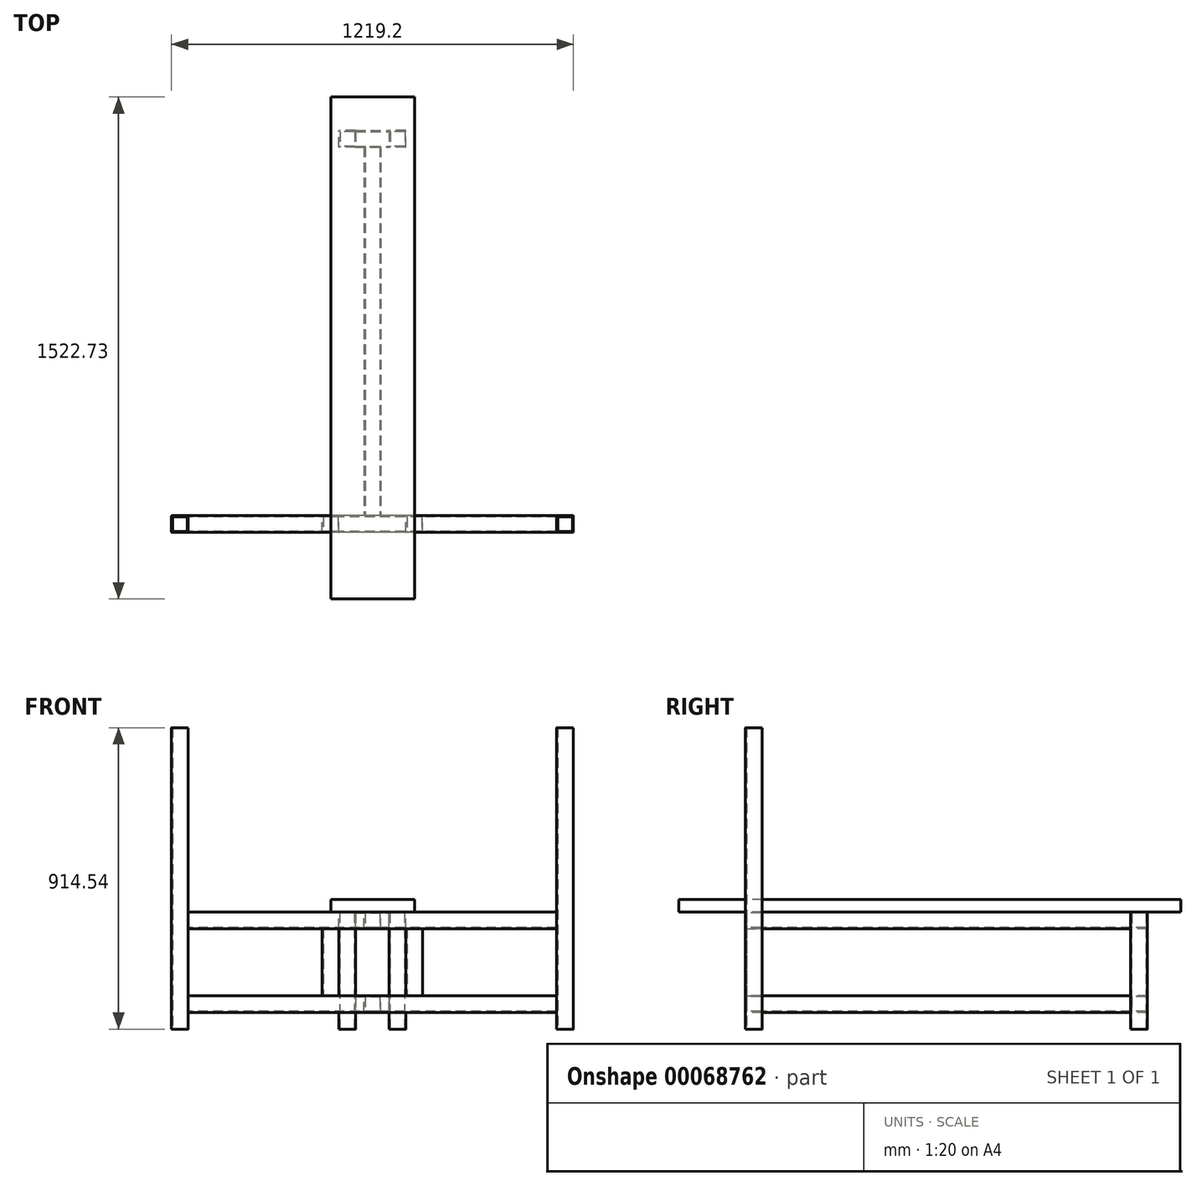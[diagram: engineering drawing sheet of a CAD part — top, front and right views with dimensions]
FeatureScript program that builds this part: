
annotation { "Feature Type Name" : "Feature", "Feature Type Description" : "" }
export const myFeature = defineFeature(function(context is Context, id is Id, definition is map)
    precondition{}
    {
        {
            var Q0;
            Q0=qCreatedBy(makeId("Front.planeOp"),FACE);
            var sketch = newSketch(context, id + "F0", { "sketchPlane" : qUnion([Q0])});
            skLineSegment(sketch, "E0.rect.bottom", {"start": v(24.13, -25.4) * mm, "end": v(-24.13, -25.4) * mm});
            skLineSegment(sketch, "E0.rect.top", {"start": v(24.13, 25.4) * mm, "end": v(-24.13, 25.4) * mm});
            skLineSegment(sketch, "E0.rect.left", {"start": v(25.4, -24.13) * mm, "end": v(25.4, 24.13) * mm});
            skLineSegment(sketch, "E0.rect.right", {"start": v(-25.4, -24.13) * mm, "end": v(-25.4, 24.13) * mm});
            skPoint(sketch, "E0.rect.middle", {"position": v(0, 0) * mm});
            skPoint(sketch, "E1.visualSharp", {"position": v(-25.4, 25.4) * mm});
            skArc(sketch, "E1.filletArc", {"start": v(-24.13, 25.4) * mm, "mid": v(-25.03, 25.03) * mm, "end": v(-25.4, 24.13) * mm});
            skPoint(sketch, "E2.visualSharp", {"position": v(25.4, 25.4) * mm});
            skArc(sketch, "E2.filletArc", {"start": v(25.4, 24.13) * mm, "mid": v(25.03, 25.03) * mm, "end": v(24.13, 25.4) * mm});
            skPoint(sketch, "E3.visualSharp", {"position": v(25.4, -25.4) * mm});
            skArc(sketch, "E3.filletArc", {"start": v(24.13, -25.4) * mm, "mid": v(25.03, -25.03) * mm, "end": v(25.4, -24.13) * mm});
            skPoint(sketch, "E4.visualSharp", {"position": v(-25.4, -25.4) * mm});
            skArc(sketch, "E4.filletArc", {"start": v(-25.4, -24.13) * mm, "mid": v(-25.03, -25.03) * mm, "end": v(-24.13, -25.4) * mm});
            skLineSegment(sketch, "E5.bottom", {"start": v(21.08, 22.35) * mm, "end": v(-21.08, 22.35) * mm});
            skLineSegment(sketch, "E5.top", {"start": v(21.08, -22.35) * mm, "end": v(-21.08, -22.35) * mm});
            skLineSegment(sketch, "E5.left", {"start": v(22.35, 21.08) * mm, "end": v(22.35, -21.08) * mm});
            skLineSegment(sketch, "E5.right", {"start": v(-22.35, 21.08) * mm, "end": v(-22.35, -21.08) * mm});
            skPoint(sketch, "E6.visualSharp", {"position": v(-22.35, 22.35) * mm});
            skArc(sketch, "E6.filletArc", {"start": v(-21.08, 22.35) * mm, "mid": v(-21.98, 21.98) * mm, "end": v(-22.35, 21.08) * mm});
            skPoint(sketch, "E7.visualSharp", {"position": v(22.35, 22.35) * mm});
            skArc(sketch, "E7.filletArc", {"start": v(22.35, 21.08) * mm, "mid": v(21.98, 21.98) * mm, "end": v(21.08, 22.35) * mm});
            skPoint(sketch, "E8.visualSharp", {"position": v(22.35, -22.35) * mm});
            skArc(sketch, "E8.filletArc", {"start": v(21.08, -22.35) * mm, "mid": v(21.98, -21.98) * mm, "end": v(22.35, -21.08) * mm});
            skPoint(sketch, "E9.visualSharp", {"position": v(-22.35, -22.35) * mm});
            skArc(sketch, "E9.filletArc", {"start": v(-22.35, -21.08) * mm, "mid": v(-21.98, -21.98) * mm, "end": v(-21.08, -22.35) * mm});
            skSolve(sketch);
        }
        {
            var Q0;
            Q0=makeQuery(id+"F0.imprint","IMPRINT",FACE,{"disambiguationData":[TD([[makeQuery(id+"F0.imprint","IMPRINT",EDGE,{"derivedFrom":sQuery(id+"F0.wireOp",EDGE,"E0.rect.bottom")}),-1.0]])]});
            extrude(context, id + "F1", {"entities" : qUnion([Q0]), "oppositeDirection" : true, "depth" : 1117.6 * mm});
        }
        {
            var Q0;
            Q0=makeQuery(id+"F1.opExtrude","SWEPT_FACE",FACE,{"disambiguationData":[OSD([sQuery(id+"F0.wireOp",EDGE,"E0.rect.left")])]});
            var sketch = newSketch(context, id + "F2", { "sketchPlane" : qUnion([Q0])});
            skLineSegment(sketch, "E10", {"start": v(1116.6, 0) * mm, "end": v(1169.4, 0) * mm, "construction": true});
            skPoint(sketch, "E10.startSnap0", {"position": v(1117.6, 0) * mm});
            skLineSegment(sketch, "E11", {"start": v(1143, 0) * mm, "end": v(1143, 22.98) * mm, "construction": true});
            skLineSegment(sketch, "E12.rect.bottom", {"start": v(1167.13, -25.4) * mm, "end": v(1118.87, -25.4) * mm});
            skLineSegment(sketch, "E12.rect.top", {"start": v(1167.13, 25.4) * mm, "end": v(1118.87, 25.4) * mm});
            skLineSegment(sketch, "E12.rect.left", {"start": v(1168.4, -24.13) * mm, "end": v(1168.4, 24.13) * mm});
            skLineSegment(sketch, "E12.rect.right", {"start": v(1117.6, -24.13) * mm, "end": v(1117.6, 24.13) * mm});
            skPoint(sketch, "E12.rect.middle", {"position": v(1143, 0) * mm});
            skPoint(sketch, "E13.visualSharp", {"position": v(1117.6, 25.4) * mm});
            skArc(sketch, "E13.filletArc", {"start": v(1118.87, 25.4) * mm, "mid": v(1117.97, 25.03) * mm, "end": v(1117.6, 24.13) * mm});
            skPoint(sketch, "E14.visualSharp", {"position": v(1168.4, 25.4) * mm});
            skArc(sketch, "E14.filletArc", {"start": v(1168.4, 24.13) * mm, "mid": v(1168.03, 25.03) * mm, "end": v(1167.13, 25.4) * mm});
            skPoint(sketch, "E15.visualSharp", {"position": v(1168.4, -25.4) * mm});
            skArc(sketch, "E15.filletArc", {"start": v(1167.13, -25.4) * mm, "mid": v(1168.03, -25.03) * mm, "end": v(1168.4, -24.13) * mm});
            skPoint(sketch, "E16.visualSharp", {"position": v(1117.6, -25.4) * mm});
            skArc(sketch, "E16.filletArc", {"start": v(1117.6, -24.13) * mm, "mid": v(1117.97, -25.03) * mm, "end": v(1118.87, -25.4) * mm});
            skLineSegment(sketch, "E17.bottom", {"start": v(1164.08, 22.35) * mm, "end": v(1121.92, 22.35) * mm});
            skLineSegment(sketch, "E17.top", {"start": v(1164.08, -22.35) * mm, "end": v(1121.92, -22.35) * mm});
            skLineSegment(sketch, "E17.left", {"start": v(1165.35, 21.08) * mm, "end": v(1165.35, -21.08) * mm});
            skLineSegment(sketch, "E17.right", {"start": v(1120.65, 21.08) * mm, "end": v(1120.65, -21.08) * mm});
            skPoint(sketch, "E18.visualSharp", {"position": v(1120.65, 22.35) * mm});
            skArc(sketch, "E18.filletArc", {"start": v(1121.92, 22.35) * mm, "mid": v(1121.02, 21.98) * mm, "end": v(1120.65, 21.08) * mm});
            skPoint(sketch, "E19.visualSharp", {"position": v(1165.35, 22.35) * mm});
            skArc(sketch, "E19.filletArc", {"start": v(1165.35, 21.08) * mm, "mid": v(1164.98, 21.98) * mm, "end": v(1164.08, 22.35) * mm});
            skPoint(sketch, "E20.visualSharp", {"position": v(1165.35, -22.35) * mm});
            skArc(sketch, "E20.filletArc", {"start": v(1164.08, -22.35) * mm, "mid": v(1164.98, -21.98) * mm, "end": v(1165.35, -21.08) * mm});
            skPoint(sketch, "E21.visualSharp", {"position": v(1120.65, -22.35) * mm});
            skArc(sketch, "E21.filletArc", {"start": v(1120.65, -21.08) * mm, "mid": v(1121.02, -21.98) * mm, "end": v(1121.92, -22.35) * mm});
            skSolve(sketch);
        }
        {
            var Q0;
            Q0=makeQuery(id+"F2.imprint","IMPRINT",FACE,{"disambiguationData":[TD([[makeQuery(id+"F2.imprint","IMPRINT",EDGE,{"derivedFrom":sQuery(id+"F2.wireOp",EDGE,"E12.rect.bottom")}),-1.0]])]});
            extrude(context, id + "F3", {"entities" : qUnion([Q0]), "oppositeDirection" : true, "depth" : 76.2 * mm});
        }
        {
            var Q0;
            Q0=makeQuery(id+"F3.opExtrude","CAP_FACE",FACE,{"disambiguationData":[OSD([sQuery(id+"F2.wireOp",EDGE,"E12.rect.bottom"),sQuery(id+"F2.wireOp",EDGE,"E12.rect.top"),sQuery(id+"F2.wireOp",EDGE,"E12.rect.left"),sQuery(id+"F2.wireOp",EDGE,"E12.rect.right"),sQuery(id+"F2.wireOp",EDGE,"E13.filletArc"),sQuery(id+"F2.wireOp",EDGE,"E14.filletArc"),sQuery(id+"F2.wireOp",EDGE,"E15.filletArc"),sQuery(id+"F2.wireOp",EDGE,"E16.filletArc"),sQuery(id+"F2.wireOp",EDGE,"E17.bottom"),sQuery(id+"F2.wireOp",EDGE,"E17.top"),sQuery(id+"F2.wireOp",EDGE,"E17.left"),sQuery(id+"F2.wireOp",EDGE,"E17.right"),sQuery(id+"F2.wireOp",EDGE,"E18.filletArc"),sQuery(id+"F2.wireOp",EDGE,"E19.filletArc"),sQuery(id+"F2.wireOp",EDGE,"E20.filletArc"),sQuery(id+"F2.wireOp",EDGE,"E21.filletArc")])],"isStart":true});
            extrude(context, id + "F4", {"entities" : qUnion([Q0]), "operationType" : NewBodyOperationType.ADD, "depth" : 25.4 * mm});
        }
        {
            var Q0;
            Q0=qCreatedBy(makeId("Front.planeOp"),FACE);
            var sketch = newSketch(context, id + "F5", { "sketchPlane" : qUnion([Q0])});
            skLineSegment(sketch, "E22.rect.bottom", {"start": v(24.13, 228.6) * mm, "end": v(-24.13, 228.6) * mm});
            skLineSegment(sketch, "E22.rect.top", {"start": v(24.13, 279.4) * mm, "end": v(-24.13, 279.4) * mm});
            skLineSegment(sketch, "E22.rect.left", {"start": v(25.4, 229.87) * mm, "end": v(25.4, 278.13) * mm});
            skLineSegment(sketch, "E22.rect.right", {"start": v(-25.4, 229.87) * mm, "end": v(-25.4, 278.13) * mm});
            skPoint(sketch, "E22.rect.middle", {"position": v(0, 254) * mm});
            skPoint(sketch, "E23.visualSharp", {"position": v(-25.4, 279.4) * mm});
            skArc(sketch, "E23.filletArc", {"start": v(-24.13, 279.4) * mm, "mid": v(-25.03, 279.03) * mm, "end": v(-25.4, 278.13) * mm});
            skPoint(sketch, "E24.visualSharp", {"position": v(25.4, 279.4) * mm});
            skArc(sketch, "E24.filletArc", {"start": v(25.4, 278.13) * mm, "mid": v(25.03, 279.03) * mm, "end": v(24.13, 279.4) * mm});
            skPoint(sketch, "E25.visualSharp", {"position": v(25.4, 228.6) * mm});
            skArc(sketch, "E25.filletArc", {"start": v(24.13, 228.6) * mm, "mid": v(25.03, 228.97) * mm, "end": v(25.4, 229.87) * mm});
            skPoint(sketch, "E26.visualSharp", {"position": v(-25.4, 228.6) * mm});
            skArc(sketch, "E26.filletArc", {"start": v(-25.4, 229.87) * mm, "mid": v(-25.03, 228.97) * mm, "end": v(-24.13, 228.6) * mm});
            skLineSegment(sketch, "E27.bottom", {"start": v(21.08, 276.35) * mm, "end": v(-21.08, 276.35) * mm});
            skLineSegment(sketch, "E27.top", {"start": v(21.08, 231.65) * mm, "end": v(-21.08, 231.65) * mm});
            skLineSegment(sketch, "E27.left", {"start": v(22.35, 275.08) * mm, "end": v(22.35, 232.92) * mm});
            skLineSegment(sketch, "E27.right", {"start": v(-22.35, 275.08) * mm, "end": v(-22.35, 232.92) * mm});
            skPoint(sketch, "E28.visualSharp", {"position": v(-22.35, 276.35) * mm});
            skArc(sketch, "E28.filletArc", {"start": v(-21.08, 276.35) * mm, "mid": v(-21.98, 275.98) * mm, "end": v(-22.35, 275.08) * mm});
            skPoint(sketch, "E29.visualSharp", {"position": v(22.35, 276.35) * mm});
            skArc(sketch, "E29.filletArc", {"start": v(22.35, 275.08) * mm, "mid": v(21.98, 275.98) * mm, "end": v(21.08, 276.35) * mm});
            skPoint(sketch, "E30.visualSharp", {"position": v(22.35, 231.65) * mm});
            skArc(sketch, "E30.filletArc", {"start": v(21.08, 231.65) * mm, "mid": v(21.98, 232.02) * mm, "end": v(22.35, 232.92) * mm});
            skPoint(sketch, "E31.visualSharp", {"position": v(-22.35, 231.65) * mm});
            skArc(sketch, "E31.filletArc", {"start": v(-22.35, 232.92) * mm, "mid": v(-21.98, 232.02) * mm, "end": v(-21.08, 231.65) * mm});
            skLineSegment(sketch, "E32", {"start": v(0, 254) * mm, "end": v(-44.9, 254) * mm});
            skSolve(sketch);
        }
        {
            var Q0;
            Q0=makeQuery(id+"F5.imprint","IMPRINT",FACE,{"disambiguationData":[TD([[makeQuery(id+"F5.imprint","IMPRINT",EDGE,{"derivedFrom":sQuery(id+"F5.wireOp",EDGE,"E22.rect.bottom")}),-1.0]])]});
            extrude(context, id + "F6", {"entities" : qUnion([Q0]), "oppositeDirection" : true, "depth" : 1117.6 * mm});
        }
        {
            var Q0;
            Q0=makeQuery(id+"F4.opExtrude","CAP_FACE",FACE,{"disambiguationData":[OSD([sQuery(id+"F2.wireOp",EDGE,"E12.rect.bottom"),sQuery(id+"F2.wireOp",EDGE,"E12.rect.top"),sQuery(id+"F2.wireOp",EDGE,"E12.rect.left"),sQuery(id+"F2.wireOp",EDGE,"E12.rect.right"),sQuery(id+"F2.wireOp",EDGE,"E13.filletArc"),sQuery(id+"F2.wireOp",EDGE,"E14.filletArc"),sQuery(id+"F2.wireOp",EDGE,"E15.filletArc"),sQuery(id+"F2.wireOp",EDGE,"E16.filletArc"),sQuery(id+"F2.wireOp",EDGE,"E17.bottom"),sQuery(id+"F2.wireOp",EDGE,"E17.top"),sQuery(id+"F2.wireOp",EDGE,"E17.left"),sQuery(id+"F2.wireOp",EDGE,"E17.right"),sQuery(id+"F2.wireOp",EDGE,"E18.filletArc"),sQuery(id+"F2.wireOp",EDGE,"E19.filletArc"),sQuery(id+"F2.wireOp",EDGE,"E20.filletArc"),sQuery(id+"F2.wireOp",EDGE,"E21.filletArc")])],"isStart":false});
            var sketch = newSketch(context, id + "F7", { "sketchPlane" : qUnion([Q0])});
            skLineSegment(sketch, "E33.rect.bottom", {"start": v(1167.13, 228.6) * mm, "end": v(1118.87, 228.6) * mm});
            skLineSegment(sketch, "E33.rect.top", {"start": v(1167.13, 279.4) * mm, "end": v(1118.87, 279.4) * mm});
            skLineSegment(sketch, "E33.rect.left", {"start": v(1168.4, 229.87) * mm, "end": v(1168.4, 278.13) * mm});
            skLineSegment(sketch, "E33.rect.right", {"start": v(1117.6, 229.87) * mm, "end": v(1117.6, 278.13) * mm});
            skPoint(sketch, "E33.rect.middle", {"position": v(1143, 254) * mm});
            skPoint(sketch, "E34.visualSharp", {"position": v(1117.6, 279.4) * mm});
            skArc(sketch, "E34.filletArc", {"start": v(1118.87, 279.4) * mm, "mid": v(1117.97, 279.03) * mm, "end": v(1117.6, 278.13) * mm});
            skPoint(sketch, "E35.visualSharp", {"position": v(1168.4, 279.4) * mm});
            skArc(sketch, "E35.filletArc", {"start": v(1168.4, 278.13) * mm, "mid": v(1168.03, 279.03) * mm, "end": v(1167.13, 279.4) * mm});
            skPoint(sketch, "E36.visualSharp", {"position": v(1168.4, 228.6) * mm});
            skArc(sketch, "E36.filletArc", {"start": v(1167.13, 228.6) * mm, "mid": v(1168.03, 228.97) * mm, "end": v(1168.4, 229.87) * mm});
            skPoint(sketch, "E37.visualSharp", {"position": v(1117.6, 228.6) * mm});
            skArc(sketch, "E37.filletArc", {"start": v(1117.6, 229.87) * mm, "mid": v(1117.97, 228.97) * mm, "end": v(1118.87, 228.6) * mm});
            skLineSegment(sketch, "E38.bottom", {"start": v(1164.08, 276.35) * mm, "end": v(1121.92, 276.35) * mm});
            skLineSegment(sketch, "E38.top", {"start": v(1164.08, 231.65) * mm, "end": v(1121.92, 231.65) * mm});
            skLineSegment(sketch, "E38.left", {"start": v(1165.35, 275.08) * mm, "end": v(1165.35, 232.92) * mm});
            skLineSegment(sketch, "E38.right", {"start": v(1120.65, 275.08) * mm, "end": v(1120.65, 232.92) * mm});
            skPoint(sketch, "E39.visualSharp", {"position": v(1120.65, 276.35) * mm});
            skArc(sketch, "E39.filletArc", {"start": v(1121.92, 276.35) * mm, "mid": v(1121.02, 275.98) * mm, "end": v(1120.65, 275.08) * mm});
            skPoint(sketch, "E40.visualSharp", {"position": v(1165.35, 276.35) * mm});
            skArc(sketch, "E40.filletArc", {"start": v(1165.35, 275.08) * mm, "mid": v(1164.98, 275.98) * mm, "end": v(1164.08, 276.35) * mm});
            skPoint(sketch, "E41.visualSharp", {"position": v(1165.35, 231.65) * mm});
            skArc(sketch, "E41.filletArc", {"start": v(1164.08, 231.65) * mm, "mid": v(1164.98, 232.02) * mm, "end": v(1165.35, 232.92) * mm});
            skPoint(sketch, "E42.visualSharp", {"position": v(1120.65, 231.65) * mm});
            skArc(sketch, "E42.filletArc", {"start": v(1120.65, 232.92) * mm, "mid": v(1121.02, 232.02) * mm, "end": v(1121.92, 231.65) * mm});
            skSolve(sketch);
        }
        {
            var Q0;
            Q0=makeQuery(id+"F7.imprint","IMPRINT",FACE,{"disambiguationData":[TD([[makeQuery(id+"F7.imprint","IMPRINT",EDGE,{"derivedFrom":sQuery(id+"F7.wireOp",EDGE,"E33.rect.top")}),1.0]])]});
            extrude(context, id + "F8", {"entities" : qUnion([Q0]), "oppositeDirection" : true, "depth" : 101.6 * mm});
        }
        {
            var Q0;
            Q0=makeQuery(id+"F8.opExtrude","SWEPT_FACE",FACE,{"disambiguationData":[OSD([sQuery(id+"F7.wireOp",EDGE,"E33.rect.top")])]});
            var sketch = newSketch(context, id + "F9", { "sketchPlane" : qUnion([Q0])});
            skPoint(sketch, "E43.endSnap0", {"position": v(50.8, 1143) * mm});
            skPoint(sketch, "E44", {"position": v(-76.2, 1143) * mm});
            skPoint(sketch, "E45", {"position": v(76.2, 1143) * mm});
            skLineSegment(sketch, "E46.rect.bottom", {"start": v(-52.07, 1117.6) * mm, "end": v(-100.33, 1117.6) * mm});
            skLineSegment(sketch, "E46.rect.top", {"start": v(-52.07, 1168.4) * mm, "end": v(-100.33, 1168.4) * mm});
            skLineSegment(sketch, "E46.rect.left", {"start": v(-50.8, 1118.87) * mm, "end": v(-50.8, 1167.13) * mm});
            skLineSegment(sketch, "E46.rect.right", {"start": v(-101.6, 1118.87) * mm, "end": v(-101.6, 1167.13) * mm});
            skPoint(sketch, "E47.visualSharp", {"position": v(-101.6, 1168.4) * mm});
            skArc(sketch, "E47.filletArc", {"start": v(-100.33, 1168.4) * mm, "mid": v(-101.23, 1168.03) * mm, "end": v(-101.6, 1167.13) * mm});
            skPoint(sketch, "E48.visualSharp", {"position": v(-50.8, 1168.4) * mm});
            skArc(sketch, "E48.filletArc", {"start": v(-50.8, 1167.13) * mm, "mid": v(-51.17, 1168.03) * mm, "end": v(-52.07, 1168.4) * mm});
            skPoint(sketch, "E49.visualSharp", {"position": v(-50.8, 1117.6) * mm});
            skArc(sketch, "E49.filletArc", {"start": v(-52.07, 1117.6) * mm, "mid": v(-51.17, 1117.97) * mm, "end": v(-50.8, 1118.87) * mm});
            skPoint(sketch, "E50.visualSharp", {"position": v(-101.6, 1117.6) * mm});
            skArc(sketch, "E50.filletArc", {"start": v(-101.6, 1118.87) * mm, "mid": v(-101.23, 1117.97) * mm, "end": v(-100.33, 1117.6) * mm});
            skLineSegment(sketch, "E51.bottom", {"start": v(-55.12, 1165.35) * mm, "end": v(-97.28, 1165.35) * mm});
            skLineSegment(sketch, "E51.top", {"start": v(-55.12, 1120.65) * mm, "end": v(-97.28, 1120.65) * mm});
            skLineSegment(sketch, "E51.left", {"start": v(-53.85, 1164.08) * mm, "end": v(-53.85, 1121.92) * mm});
            skLineSegment(sketch, "E51.right", {"start": v(-98.55, 1164.08) * mm, "end": v(-98.55, 1121.92) * mm});
            skPoint(sketch, "E52.visualSharp", {"position": v(-98.55, 1165.35) * mm});
            skArc(sketch, "E52.filletArc", {"start": v(-97.28, 1165.35) * mm, "mid": v(-98.18, 1164.98) * mm, "end": v(-98.55, 1164.08) * mm});
            skPoint(sketch, "E53.visualSharp", {"position": v(-53.85, 1165.35) * mm});
            skArc(sketch, "E53.filletArc", {"start": v(-53.85, 1164.08) * mm, "mid": v(-54.22, 1164.98) * mm, "end": v(-55.12, 1165.35) * mm});
            skPoint(sketch, "E54.visualSharp", {"position": v(-53.85, 1120.65) * mm});
            skArc(sketch, "E54.filletArc", {"start": v(-55.12, 1120.65) * mm, "mid": v(-54.22, 1121.02) * mm, "end": v(-53.85, 1121.92) * mm});
            skPoint(sketch, "E55.visualSharp", {"position": v(-98.55, 1120.65) * mm});
            skArc(sketch, "E55.filletArc", {"start": v(-98.55, 1121.92) * mm, "mid": v(-98.18, 1121.02) * mm, "end": v(-97.28, 1120.65) * mm});
            skLineSegment(sketch, "E56.rect.bottom", {"start": v(100.33, 1117.6) * mm, "end": v(52.04, 1117.6) * mm});
            skLineSegment(sketch, "E56.rect.top", {"start": v(100.33, 1168.4) * mm, "end": v(52.04, 1168.4) * mm});
            skLineSegment(sketch, "E56.rect.left", {"start": v(101.6, 1118.87) * mm, "end": v(101.6, 1167.13) * mm});
            skLineSegment(sketch, "E56.rect.right", {"start": v(50.77, 1118.87) * mm, "end": v(50.77, 1167.13) * mm});
            skPoint(sketch, "E56.rect.middle", {"position": v(76.18, 1143) * mm});
            skPoint(sketch, "E57.visualSharp", {"position": v(50.77, 1168.4) * mm});
            skArc(sketch, "E57.filletArc", {"start": v(52.04, 1168.4) * mm, "mid": v(51.14, 1168.03) * mm, "end": v(50.77, 1167.13) * mm});
            skPoint(sketch, "E58.visualSharp", {"position": v(101.6, 1168.4) * mm});
            skArc(sketch, "E58.filletArc", {"start": v(101.6, 1167.13) * mm, "mid": v(101.23, 1168.03) * mm, "end": v(100.33, 1168.4) * mm});
            skPoint(sketch, "E59.visualSharp", {"position": v(101.6, 1117.6) * mm});
            skArc(sketch, "E59.filletArc", {"start": v(100.33, 1117.6) * mm, "mid": v(101.23, 1117.97) * mm, "end": v(101.6, 1118.87) * mm});
            skPoint(sketch, "E60.visualSharp", {"position": v(50.77, 1117.6) * mm});
            skArc(sketch, "E60.filletArc", {"start": v(50.77, 1118.87) * mm, "mid": v(51.14, 1117.97) * mm, "end": v(52.04, 1117.6) * mm});
            skLineSegment(sketch, "E61.bottom", {"start": v(97.25, 1165.35) * mm, "end": v(55.09, 1165.35) * mm});
            skLineSegment(sketch, "E61.top", {"start": v(97.25, 1120.65) * mm, "end": v(55.09, 1120.65) * mm});
            skLineSegment(sketch, "E61.left", {"start": v(98.52, 1164.08) * mm, "end": v(98.52, 1121.92) * mm});
            skLineSegment(sketch, "E61.right", {"start": v(53.82, 1164.08) * mm, "end": v(53.82, 1121.92) * mm});
            skPoint(sketch, "E62.visualSharp", {"position": v(53.82, 1165.35) * mm});
            skArc(sketch, "E62.filletArc", {"start": v(55.09, 1165.35) * mm, "mid": v(54.19, 1164.98) * mm, "end": v(53.82, 1164.08) * mm});
            skPoint(sketch, "E63.visualSharp", {"position": v(98.52, 1165.35) * mm});
            skArc(sketch, "E63.filletArc", {"start": v(98.52, 1164.08) * mm, "mid": v(98.15, 1164.98) * mm, "end": v(97.25, 1165.35) * mm});
            skPoint(sketch, "E64.visualSharp", {"position": v(98.52, 1120.65) * mm});
            skArc(sketch, "E64.filletArc", {"start": v(97.25, 1120.65) * mm, "mid": v(98.15, 1121.02) * mm, "end": v(98.52, 1121.92) * mm});
            skPoint(sketch, "E65.visualSharp", {"position": v(53.82, 1120.65) * mm});
            skArc(sketch, "E65.filletArc", {"start": v(53.82, 1121.92) * mm, "mid": v(54.19, 1121.02) * mm, "end": v(55.09, 1120.65) * mm});
            skSolve(sketch);
        }
        {
            var Q0;
            Q0=makeQuery(id+"F9.imprint","IMPRINT",FACE,{"disambiguationData":[TD([[makeQuery(id+"F9.imprint","IMPRINT",EDGE,{"derivedFrom":sQuery(id+"F9.wireOp",EDGE,"E46.rect.bottom")}),-1.0]])]});
            var Q1;
            Q1=makeQuery(id+"F9.imprint","IMPRINT",FACE,{"disambiguationData":[TD([[makeQuery(id+"F9.imprint","IMPRINT",EDGE,{"derivedFrom":sQuery(id+"F9.wireOp",EDGE,"E56.rect.bottom")}),-1.0]])]});
            extrude(context, id + "F10", {"entities" : qUnion([Q0, Q1]), "oppositeDirection" : true, "depth" : 355.6 * mm});
        }
        {
            var Q0;
            Q0=qCreatedBy(makeId("Right.planeOp"),FACE);
            var sketch = newSketch(context, id + "F11", { "sketchPlane" : qUnion([Q0])});
            skLineSegment(sketch, "E66", {"start": v(0, 0) * mm, "end": v(-225.93, 0) * mm});
            skLineSegment(sketch, "E67", {"start": v(0, 0) * mm, "end": v(0, 287.4) * mm});
            skLineSegment(sketch, "E68", {"start": v(0, 254) * mm, "end": v(-244.97, 254) * mm});
            skLineSegment(sketch, "E69.rect.bottom", {"start": v(-1.27, -25.4) * mm, "end": v(-49.53, -25.4) * mm});
            skLineSegment(sketch, "E69.rect.top", {"start": v(-1.27, 25.4) * mm, "end": v(-49.53, 25.4) * mm});
            skLineSegment(sketch, "E69.rect.left", {"start": v(0, -24.13) * mm, "end": v(0, 24.13) * mm});
            skLineSegment(sketch, "E69.rect.right", {"start": v(-50.8, -24.13) * mm, "end": v(-50.8, 24.13) * mm});
            skPoint(sketch, "E69.rect.middle", {"position": v(-25.4, 0) * mm});
            skPoint(sketch, "E70.visualSharp", {"position": v(-50.8, 25.4) * mm});
            skArc(sketch, "E70.filletArc", {"start": v(-49.53, 25.4) * mm, "mid": v(-50.43, 25.03) * mm, "end": v(-50.8, 24.13) * mm});
            skPoint(sketch, "E71.visualSharp", {"position": v(0, 25.4) * mm});
            skArc(sketch, "E71.filletArc", {"start": v(0, 24.13) * mm, "mid": v(-0.37, 25.03) * mm, "end": v(-1.27, 25.4) * mm});
            skPoint(sketch, "E72.visualSharp", {"position": v(0, -25.4) * mm});
            skArc(sketch, "E72.filletArc", {"start": v(-1.27, -25.4) * mm, "mid": v(-0.37, -25.03) * mm, "end": v(0, -24.13) * mm});
            skPoint(sketch, "E73.visualSharp", {"position": v(-50.8, -25.4) * mm});
            skArc(sketch, "E73.filletArc", {"start": v(-50.8, -24.13) * mm, "mid": v(-50.43, -25.03) * mm, "end": v(-49.53, -25.4) * mm});
            skLineSegment(sketch, "E74.bottom", {"start": v(-4.32, 22.35) * mm, "end": v(-46.48, 22.35) * mm});
            skLineSegment(sketch, "E74.top", {"start": v(-4.32, -22.35) * mm, "end": v(-46.48, -22.35) * mm});
            skLineSegment(sketch, "E74.left", {"start": v(-3.05, 21.08) * mm, "end": v(-3.05, -21.08) * mm});
            skLineSegment(sketch, "E74.right", {"start": v(-47.75, 21.08) * mm, "end": v(-47.75, -21.08) * mm});
            skPoint(sketch, "E75.visualSharp", {"position": v(-47.75, 22.35) * mm});
            skArc(sketch, "E75.filletArc", {"start": v(-46.48, 22.35) * mm, "mid": v(-47.38, 21.98) * mm, "end": v(-47.75, 21.08) * mm});
            skPoint(sketch, "E76.visualSharp", {"position": v(-3.05, 22.35) * mm});
            skArc(sketch, "E76.filletArc", {"start": v(-3.05, 21.08) * mm, "mid": v(-3.42, 21.98) * mm, "end": v(-4.32, 22.35) * mm});
            skPoint(sketch, "E77.visualSharp", {"position": v(-3.05, -22.35) * mm});
            skArc(sketch, "E77.filletArc", {"start": v(-4.32, -22.35) * mm, "mid": v(-3.42, -21.98) * mm, "end": v(-3.05, -21.08) * mm});
            skPoint(sketch, "E78.visualSharp", {"position": v(-47.75, -22.35) * mm});
            skArc(sketch, "E78.filletArc", {"start": v(-47.75, -21.08) * mm, "mid": v(-47.38, -21.98) * mm, "end": v(-46.48, -22.35) * mm});
            skLineSegment(sketch, "E79.rect.bottom", {"start": v(-1.27, 228.74) * mm, "end": v(-49.53, 228.74) * mm});
            skLineSegment(sketch, "E79.rect.top", {"start": v(-1.27, 279.54) * mm, "end": v(-49.53, 279.54) * mm});
            skLineSegment(sketch, "E79.rect.left", {"start": v(0, 230.01) * mm, "end": v(0, 278.27) * mm});
            skLineSegment(sketch, "E79.rect.right", {"start": v(-50.8, 230.01) * mm, "end": v(-50.8, 278.27) * mm});
            skPoint(sketch, "E79.rect.middle", {"position": v(-25.4, 254.14) * mm});
            skPoint(sketch, "E80.visualSharp", {"position": v(-50.8, 279.54) * mm});
            skArc(sketch, "E80.filletArc", {"start": v(-49.53, 279.54) * mm, "mid": v(-50.43, 279.17) * mm, "end": v(-50.8, 278.27) * mm});
            skPoint(sketch, "E81.visualSharp", {"position": v(0, 279.54) * mm});
            skArc(sketch, "E81.filletArc", {"start": v(0, 278.27) * mm, "mid": v(-0.37, 279.17) * mm, "end": v(-1.27, 279.54) * mm});
            skPoint(sketch, "E82.visualSharp", {"position": v(0, 228.74) * mm});
            skArc(sketch, "E82.filletArc", {"start": v(-1.27, 228.74) * mm, "mid": v(-0.37, 229.11) * mm, "end": v(0, 230.01) * mm});
            skPoint(sketch, "E83.visualSharp", {"position": v(-50.8, 228.74) * mm});
            skArc(sketch, "E83.filletArc", {"start": v(-50.8, 230.01) * mm, "mid": v(-50.43, 229.11) * mm, "end": v(-49.53, 228.74) * mm});
            skLineSegment(sketch, "E84.bottom", {"start": v(-4.32, 276.5) * mm, "end": v(-46.48, 276.5) * mm});
            skLineSegment(sketch, "E84.top", {"start": v(-4.32, 231.79) * mm, "end": v(-46.48, 231.79) * mm});
            skLineSegment(sketch, "E84.left", {"start": v(-3.05, 275.22) * mm, "end": v(-3.05, 233.06) * mm});
            skLineSegment(sketch, "E84.right", {"start": v(-47.75, 275.22) * mm, "end": v(-47.75, 233.06) * mm});
            skPoint(sketch, "E85.visualSharp", {"position": v(-47.75, 276.5) * mm});
            skArc(sketch, "E85.filletArc", {"start": v(-46.48, 276.5) * mm, "mid": v(-47.38, 276.12) * mm, "end": v(-47.75, 275.22) * mm});
            skPoint(sketch, "E86.visualSharp", {"position": v(-3.05, 276.5) * mm});
            skArc(sketch, "E86.filletArc", {"start": v(-3.05, 275.22) * mm, "mid": v(-3.42, 276.12) * mm, "end": v(-4.32, 276.5) * mm});
            skPoint(sketch, "E87.visualSharp", {"position": v(-3.05, 231.79) * mm});
            skArc(sketch, "E87.filletArc", {"start": v(-4.32, 231.79) * mm, "mid": v(-3.42, 232.16) * mm, "end": v(-3.05, 233.06) * mm});
            skPoint(sketch, "E88.visualSharp", {"position": v(-47.75, 231.79) * mm});
            skArc(sketch, "E88.filletArc", {"start": v(-47.75, 233.06) * mm, "mid": v(-47.38, 232.16) * mm, "end": v(-46.48, 231.79) * mm});
            skSolve(sketch);
        }
        {
            var Q0;
            Q0=makeQuery(id+"F11.imprint","IMPRINT",FACE,{"disambiguationData":[TD([[makeQuery(id+"F11.imprint","IMPRINT",EDGE,{"derivedFrom":sQuery(id+"F11.wireOp",EDGE,"E79.rect.top")}),1.0]])]});
            var Q1;
            Q1=makeQuery(id+"F11.imprint","IMPRINT",FACE,{"disambiguationData":[TD([[makeQuery(id+"F11.imprint","IMPRINT",EDGE,{"derivedFrom":sQuery(id+"F11.wireOp",EDGE,"E79.rect.bottom")}),-1.0]])]});
            var Q2;
            Q2=makeQuery(id+"F11.imprint","IMPRINT",FACE,{"disambiguationData":[TD([[makeQuery(id+"F11.imprint","IMPRINT",EDGE,{"derivedFrom":sQuery(id+"F11.wireOp",EDGE,"E69.rect.top")}),1.0]])]});
            var Q3;
            Q3=makeQuery(id+"F11.imprint","IMPRINT",FACE,{"disambiguationData":[TD([[makeQuery(id+"F11.imprint","IMPRINT",EDGE,{"derivedFrom":sQuery(id+"F11.wireOp",EDGE,"E69.rect.bottom")}),-1.0]])]});
            extrude(context, id + "F12", {"entities" : qUnion([Q0, Q1, Q2, Q3]), "endBound" : BoundingType.SYMMETRIC, "depth" : 1117.6 * mm});
        }
        {
            var Q0;
            Q0=makeQuery(id+"F12.opExtrude","SWEPT_FACE",FACE,{"disambiguationData":[OSD([sQuery(id+"F11.wireOp",EDGE,"E79.rect.top")])]});
            var sketch = newSketch(context, id + "F13", { "sketchPlane" : qUnion([Q0])});
            skLineSegment(sketch, "E89", {"start": v(-558.8, -25.4) * mm, "end": v(-696.92, -25.4) * mm});
            skLineSegment(sketch, "E90", {"start": v(558.8, -25.4) * mm, "end": v(681.24, -25.4) * mm});
            skLineSegment(sketch, "E91", {"start": v(-558.8, -49.53) * mm, "end": v(-558.8, 18.38) * mm});
            skLineSegment(sketch, "E92", {"start": v(558.8, -49.53) * mm, "end": v(558.8, 39.59) * mm});
            skLineSegment(sketch, "E93.rect.bottom", {"start": v(-560.07, -50.8) * mm, "end": v(-608.33, -50.8) * mm});
            skLineSegment(sketch, "E93.rect.top", {"start": v(-560.07, 0) * mm, "end": v(-608.33, 0) * mm});
            skLineSegment(sketch, "E93.rect.left", {"start": v(-558.8, -49.53) * mm, "end": v(-558.8, -1.27) * mm});
            skLineSegment(sketch, "E93.rect.right", {"start": v(-609.6, -49.53) * mm, "end": v(-609.6, -1.27) * mm});
            skPoint(sketch, "E93.rect.middle", {"position": v(-584.2, -25.4) * mm});
            skPoint(sketch, "E94.visualSharp", {"position": v(-609.6, 0) * mm});
            skArc(sketch, "E94.filletArc", {"start": v(-608.33, 0) * mm, "mid": v(-609.23, -0.37) * mm, "end": v(-609.6, -1.27) * mm});
            skPoint(sketch, "E95.visualSharp", {"position": v(-558.8, 0) * mm});
            skArc(sketch, "E95.filletArc", {"start": v(-558.8, -1.27) * mm, "mid": v(-559.17, -0.37) * mm, "end": v(-560.07, 0) * mm});
            skPoint(sketch, "E96.visualSharp", {"position": v(-558.8, -50.8) * mm});
            skArc(sketch, "E96.filletArc", {"start": v(-560.07, -50.8) * mm, "mid": v(-559.17, -50.43) * mm, "end": v(-558.8, -49.53) * mm});
            skPoint(sketch, "E97.visualSharp", {"position": v(-609.6, -50.8) * mm});
            skArc(sketch, "E97.filletArc", {"start": v(-609.6, -49.53) * mm, "mid": v(-609.23, -50.43) * mm, "end": v(-608.33, -50.8) * mm});
            skLineSegment(sketch, "E98.bottom", {"start": v(-563.12, -3.05) * mm, "end": v(-605.28, -3.05) * mm});
            skLineSegment(sketch, "E98.top", {"start": v(-563.12, -47.75) * mm, "end": v(-605.28, -47.75) * mm});
            skLineSegment(sketch, "E98.left", {"start": v(-561.85, -4.32) * mm, "end": v(-561.85, -46.48) * mm});
            skLineSegment(sketch, "E98.right", {"start": v(-606.55, -4.32) * mm, "end": v(-606.55, -46.48) * mm});
            skPoint(sketch, "E99.visualSharp", {"position": v(-606.55, -3.05) * mm});
            skArc(sketch, "E99.filletArc", {"start": v(-605.28, -3.05) * mm, "mid": v(-606.18, -3.42) * mm, "end": v(-606.55, -4.32) * mm});
            skPoint(sketch, "E100.visualSharp", {"position": v(-561.85, -3.05) * mm});
            skArc(sketch, "E100.filletArc", {"start": v(-561.85, -4.32) * mm, "mid": v(-562.22, -3.42) * mm, "end": v(-563.12, -3.05) * mm});
            skPoint(sketch, "E101.visualSharp", {"position": v(-561.85, -47.75) * mm});
            skArc(sketch, "E101.filletArc", {"start": v(-563.12, -47.75) * mm, "mid": v(-562.22, -47.38) * mm, "end": v(-561.85, -46.48) * mm});
            skPoint(sketch, "E102.visualSharp", {"position": v(-606.55, -47.75) * mm});
            skArc(sketch, "E102.filletArc", {"start": v(-606.55, -46.48) * mm, "mid": v(-606.18, -47.38) * mm, "end": v(-605.28, -47.75) * mm});
            skLineSegment(sketch, "E103.rect.bottom", {"start": v(608.33, -50.8) * mm, "end": v(560.07, -50.8) * mm});
            skLineSegment(sketch, "E103.rect.top", {"start": v(608.33, 0) * mm, "end": v(560.07, 0) * mm});
            skLineSegment(sketch, "E103.rect.left", {"start": v(609.6, -49.53) * mm, "end": v(609.6, -1.27) * mm});
            skLineSegment(sketch, "E103.rect.right", {"start": v(558.8, -49.53) * mm, "end": v(558.8, -1.27) * mm});
            skPoint(sketch, "E103.rect.middle", {"position": v(584.2, -25.4) * mm});
            skPoint(sketch, "E104.visualSharp", {"position": v(558.8, 0) * mm});
            skArc(sketch, "E104.filletArc", {"start": v(560.07, 0) * mm, "mid": v(559.17, -0.37) * mm, "end": v(558.8, -1.27) * mm});
            skPoint(sketch, "E105.visualSharp", {"position": v(609.6, 0) * mm});
            skArc(sketch, "E105.filletArc", {"start": v(609.6, -1.27) * mm, "mid": v(609.23, -0.37) * mm, "end": v(608.33, 0) * mm});
            skPoint(sketch, "E106.visualSharp", {"position": v(609.6, -50.8) * mm});
            skArc(sketch, "E106.filletArc", {"start": v(608.33, -50.8) * mm, "mid": v(609.23, -50.43) * mm, "end": v(609.6, -49.53) * mm});
            skPoint(sketch, "E107.visualSharp", {"position": v(558.8, -50.8) * mm});
            skArc(sketch, "E107.filletArc", {"start": v(558.8, -49.53) * mm, "mid": v(559.17, -50.43) * mm, "end": v(560.07, -50.8) * mm});
            skLineSegment(sketch, "E108.bottom", {"start": v(605.28, -3.05) * mm, "end": v(563.12, -3.05) * mm});
            skLineSegment(sketch, "E108.top", {"start": v(605.28, -47.75) * mm, "end": v(563.12, -47.75) * mm});
            skLineSegment(sketch, "E108.left", {"start": v(606.55, -4.32) * mm, "end": v(606.55, -46.48) * mm});
            skLineSegment(sketch, "E108.right", {"start": v(561.85, -4.32) * mm, "end": v(561.85, -46.48) * mm});
            skPoint(sketch, "E109.visualSharp", {"position": v(561.85, -3.05) * mm});
            skArc(sketch, "E109.filletArc", {"start": v(563.12, -3.05) * mm, "mid": v(562.22, -3.42) * mm, "end": v(561.85, -4.32) * mm});
            skPoint(sketch, "E110.visualSharp", {"position": v(606.55, -3.05) * mm});
            skArc(sketch, "E110.filletArc", {"start": v(606.55, -4.32) * mm, "mid": v(606.18, -3.42) * mm, "end": v(605.28, -3.05) * mm});
            skPoint(sketch, "E111.visualSharp", {"position": v(606.55, -47.75) * mm});
            skArc(sketch, "E111.filletArc", {"start": v(605.28, -47.75) * mm, "mid": v(606.18, -47.38) * mm, "end": v(606.55, -46.48) * mm});
            skPoint(sketch, "E112.visualSharp", {"position": v(561.85, -47.75) * mm});
            skArc(sketch, "E112.filletArc", {"start": v(561.85, -46.48) * mm, "mid": v(562.22, -47.38) * mm, "end": v(563.12, -47.75) * mm});
            skSolve(sketch);
        }
        {
            var Q0;
            Q0=makeQuery(id+"F13.imprint","IMPRINT",FACE,{"disambiguationData":[TD([[makeQuery(id+"F13.imprint","IMPRINT",EDGE,{"derivedFrom":sQuery(id+"F13.wireOp",EDGE,"E93.rect.top")}),1.0]])]});
            var Q1;
            Q1=makeQuery(id+"F13.imprint","IMPRINT",FACE,{"disambiguationData":[TD([[makeQuery(id+"F13.imprint","IMPRINT",EDGE,{"derivedFrom":sQuery(id+"F13.wireOp",EDGE,"E93.rect.bottom")}),-1.0]])]});
            var Q2;
            Q2=makeQuery(id+"F13.imprint","IMPRINT",FACE,{"disambiguationData":[TD([[makeQuery(id+"F13.imprint","IMPRINT",EDGE,{"derivedFrom":sQuery(id+"F13.wireOp",EDGE,"E103.rect.top")}),1.0]])]});
            var Q3;
            Q3=makeQuery(id+"F13.imprint","IMPRINT",FACE,{"disambiguationData":[TD([[makeQuery(id+"F13.imprint","IMPRINT",EDGE,{"derivedFrom":sQuery(id+"F13.wireOp",EDGE,"E103.rect.bottom")}),-1.0]])]});
            extrude(context, id + "F14", {"entities" : qUnion([Q0, Q1, Q2, Q3]), "depth" : 558.8 * mm, "hasSecondDirection" : true, "secondDirectionOppositeDirection" : true, "secondDirectionDepth" : 355.6 * mm});
        }
        {
            var Q0;
            Q0=makeQuery(id+"F6.opExtrude","SWEPT_FACE",FACE,{"disambiguationData":[OSD([sQuery(id+"F5.wireOp",EDGE,"E22.rect.top")])]});
            var sketch = newSketch(context, id + "F15", { "sketchPlane" : qUnion([Q0])});
            skLineSegment(sketch, "E113.bottom", {"start": v(-125.73, 1270) * mm, "end": v(128.27, 1270) * mm});
            skLineSegment(sketch, "E113.top", {"start": v(-125.73, -252.73) * mm, "end": v(128.27, -252.73) * mm});
            skLineSegment(sketch, "E113.left", {"start": v(-125.73, 1270) * mm, "end": v(-125.73, -252.73) * mm});
            skLineSegment(sketch, "E113.right", {"start": v(128.27, 1270) * mm, "end": v(128.27, -252.73) * mm});
            skSolve(sketch);
        }
        {
            var Q0;
            Q0=makeQuery(id+"F15.imprint","IMPRINT",FACE,{"disambiguationData":[TD([[makeQuery(id+"F15.imprint","IMPRINT",EDGE,{"derivedFrom":sQuery(id+"F15.wireOp",EDGE,"E113.bottom")}),-1.0]])]});
            var Q1;
            {var subQ0=sQuery(id+"F5.wireOp",EDGE,"E22.rect.top");Q1=makeQuery(id+"F15.imprint","IMPRINT",FACE,{"disambiguationData":[TD([[makeQuery(id+"F15.imprint","IMPRINT",EDGE,{"derivedFrom":makeQuery(id+"F6.opExtrude","CAP_EDGE",EDGE,{"disambiguationData":[OSD([subQ0])],"isStart":true})}),-1.0]])]});}
            extrude(context, id + "F16", {"entities" : qUnion([Q0, Q1]), "depth" : 38.1 * mm});
        }
        {
            var Q0;
            Q0=makeQuery(id+"F12.opExtrude","SWEPT_FACE",FACE,{"disambiguationData":[OSD([sQuery(id+"F11.wireOp",EDGE,"E69.rect.top")])]});
            cPlane(context, id + "F17", {"entities" : qUnion([Q0]), "cplaneType" : CPlaneType.OFFSET, "offset" : 0 * mm, "width" : 152.4 * mm, "height" : 152.4 * mm});
        }
        {
            var Q0;
            Q0=qCreatedBy(id+"F17.planeOp",FACE);
            var sketch = newSketch(context, id + "F18", { "sketchPlane" : qUnion([Q0])});
            skLineSegment(sketch, "E114", {"start": v(0, 0) * mm, "end": v(-101.6, 0) * mm});
            skLineSegment(sketch, "E115", {"start": v(0, 0) * mm, "end": v(0, -50.8) * mm});
            skLineSegment(sketch, "E116.rect.bottom", {"start": v(-102.87, -50.8) * mm, "end": v(-151.13, -50.8) * mm});
            skLineSegment(sketch, "E116.rect.top", {"start": v(-102.87, 0) * mm, "end": v(-151.13, 0) * mm});
            skLineSegment(sketch, "E116.rect.left", {"start": v(-101.6, -49.53) * mm, "end": v(-101.6, -1.27) * mm});
            skLineSegment(sketch, "E116.rect.right", {"start": v(-152.4, -49.53) * mm, "end": v(-152.4, -1.27) * mm});
            skPoint(sketch, "E116.rect.middle", {"position": v(-127, -25.4) * mm});
            skPoint(sketch, "E117.visualSharp", {"position": v(-152.4, 0) * mm});
            skArc(sketch, "E117.filletArc", {"start": v(-151.13, 0) * mm, "mid": v(-152.03, -0.37) * mm, "end": v(-152.4, -1.27) * mm});
            skPoint(sketch, "E118.visualSharp", {"position": v(-101.6, 0) * mm});
            skArc(sketch, "E118.filletArc", {"start": v(-101.6, -1.27) * mm, "mid": v(-101.97, -0.37) * mm, "end": v(-102.87, 0) * mm});
            skPoint(sketch, "E119.visualSharp", {"position": v(-101.6, -50.8) * mm});
            skArc(sketch, "E119.filletArc", {"start": v(-102.87, -50.8) * mm, "mid": v(-101.97, -50.43) * mm, "end": v(-101.6, -49.53) * mm});
            skPoint(sketch, "E120.visualSharp", {"position": v(-152.4, -50.8) * mm});
            skArc(sketch, "E120.filletArc", {"start": v(-152.4, -49.53) * mm, "mid": v(-152.03, -50.43) * mm, "end": v(-151.13, -50.8) * mm});
            skLineSegment(sketch, "E121.bottom", {"start": v(-105.92, -3.04) * mm, "end": v(-148.08, -3.04) * mm});
            skLineSegment(sketch, "E121.top", {"start": v(-105.92, -47.74) * mm, "end": v(-148.08, -47.74) * mm});
            skLineSegment(sketch, "E121.left", {"start": v(-104.65, -4.31) * mm, "end": v(-104.65, -46.47) * mm});
            skLineSegment(sketch, "E121.right", {"start": v(-149.35, -4.31) * mm, "end": v(-149.35, -46.47) * mm});
            skPoint(sketch, "E122.visualSharp", {"position": v(-149.35, -3.04) * mm});
            skArc(sketch, "E122.filletArc", {"start": v(-148.08, -3.04) * mm, "mid": v(-148.98, -3.41) * mm, "end": v(-149.35, -4.31) * mm});
            skPoint(sketch, "E123.visualSharp", {"position": v(-104.65, -3.04) * mm});
            skArc(sketch, "E123.filletArc", {"start": v(-104.65, -4.31) * mm, "mid": v(-105.02, -3.41) * mm, "end": v(-105.92, -3.04) * mm});
            skPoint(sketch, "E124.visualSharp", {"position": v(-104.65, -47.74) * mm});
            skArc(sketch, "E124.filletArc", {"start": v(-105.92, -47.74) * mm, "mid": v(-105.02, -47.37) * mm, "end": v(-104.65, -46.47) * mm});
            skPoint(sketch, "E125.visualSharp", {"position": v(-149.35, -47.74) * mm});
            skArc(sketch, "E125.filletArc", {"start": v(-149.35, -46.47) * mm, "mid": v(-148.98, -47.37) * mm, "end": v(-148.08, -47.74) * mm});
            skLineSegment(sketch, "E126", {"start": v(127, 11.28) * mm, "end": v(127, -81.2) * mm});
            skLineSegment(sketch, "E127", {"start": v(0, -25.4) * mm, "end": v(192.46, -25.4) * mm});
            skPoint(sketch, "E128", {"position": v(127, -25.4) * mm});
            skLineSegment(sketch, "E129.rect.bottom", {"start": v(151.13, -50.8) * mm, "end": v(102.87, -50.8) * mm});
            skLineSegment(sketch, "E129.rect.top", {"start": v(151.13, 0) * mm, "end": v(102.87, 0) * mm});
            skLineSegment(sketch, "E129.rect.left", {"start": v(152.4, -49.53) * mm, "end": v(152.4, -1.27) * mm});
            skLineSegment(sketch, "E129.rect.right", {"start": v(101.6, -49.53) * mm, "end": v(101.6, -1.27) * mm});
            skPoint(sketch, "E130.visualSharp", {"position": v(101.6, 0) * mm});
            skArc(sketch, "E130.filletArc", {"start": v(102.87, 0) * mm, "mid": v(101.97, -0.37) * mm, "end": v(101.6, -1.27) * mm});
            skPoint(sketch, "E131.visualSharp", {"position": v(152.4, 0) * mm});
            skArc(sketch, "E131.filletArc", {"start": v(152.4, -1.27) * mm, "mid": v(152.03, -0.37) * mm, "end": v(151.13, 0) * mm});
            skPoint(sketch, "E132.visualSharp", {"position": v(152.4, -50.8) * mm});
            skArc(sketch, "E132.filletArc", {"start": v(151.13, -50.8) * mm, "mid": v(152.03, -50.43) * mm, "end": v(152.4, -49.53) * mm});
            skPoint(sketch, "E133.visualSharp", {"position": v(101.6, -50.8) * mm});
            skArc(sketch, "E133.filletArc", {"start": v(101.6, -49.53) * mm, "mid": v(101.97, -50.43) * mm, "end": v(102.87, -50.8) * mm});
            skLineSegment(sketch, "E134.bottom", {"start": v(148.06, -3.36) * mm, "end": v(105.9, -3.36) * mm});
            skLineSegment(sketch, "E134.top", {"start": v(148.06, -48.07) * mm, "end": v(105.9, -48.07) * mm});
            skLineSegment(sketch, "E134.left", {"start": v(149.33, -4.63) * mm, "end": v(149.33, -46.8) * mm});
            skLineSegment(sketch, "E134.right", {"start": v(104.62, -4.63) * mm, "end": v(104.62, -46.8) * mm});
            skPoint(sketch, "E135.visualSharp", {"position": v(104.62, -3.36) * mm});
            skArc(sketch, "E135.filletArc", {"start": v(105.9, -3.36) * mm, "mid": v(105, -3.74) * mm, "end": v(104.62, -4.63) * mm});
            skPoint(sketch, "E136.visualSharp", {"position": v(149.33, -3.36) * mm});
            skArc(sketch, "E136.filletArc", {"start": v(149.33, -4.63) * mm, "mid": v(148.96, -3.74) * mm, "end": v(148.06, -3.36) * mm});
            skPoint(sketch, "E137.visualSharp", {"position": v(149.33, -48.07) * mm});
            skArc(sketch, "E137.filletArc", {"start": v(148.06, -48.07) * mm, "mid": v(148.96, -47.7) * mm, "end": v(149.33, -46.8) * mm});
            skPoint(sketch, "E138.visualSharp", {"position": v(104.62, -48.07) * mm});
            skArc(sketch, "E138.filletArc", {"start": v(104.62, -46.8) * mm, "mid": v(105, -47.7) * mm, "end": v(105.9, -48.07) * mm});
            skSolve(sketch);
        }
        {
            var Q0;
            Q0=makeQuery(id+"F18.imprint","IMPRINT",FACE,{"disambiguationData":[TD([[makeQuery(id+"F18.imprint","IMPRINT",EDGE,{"derivedFrom":sQuery(id+"F18.wireOp",EDGE,"E116.rect.bottom")}),-1.0]])]});
            var Q1;
            {var subQ0=sQuery(id+"F18.wireOp",EDGE,"E131.filletArc");Q1=makeQuery(id+"F18.imprint","IMPRINT",FACE,{"disambiguationData":[TD([[makeQuery(id+"F18.imprint","IMPRINT",EDGE,{"derivedFrom":subQ0}),1.0]])]});}
            var Q2;
            {var subQ0=sQuery(id+"F18.wireOp",EDGE,"E130.filletArc");Q2=makeQuery(id+"F18.imprint","IMPRINT",FACE,{"disambiguationData":[TD([[makeQuery(id+"F18.imprint","IMPRINT",EDGE,{"derivedFrom":subQ0}),1.0]])]});}
            var Q3;
            {var subQ0=sQuery(id+"F18.wireOp",EDGE,"E133.filletArc");Q3=makeQuery(id+"F18.imprint","IMPRINT",FACE,{"disambiguationData":[TD([[makeQuery(id+"F18.imprint","IMPRINT",EDGE,{"derivedFrom":subQ0}),1.0]])]});}
            var Q4;
            {var subQ0=sQuery(id+"F18.wireOp",EDGE,"E132.filletArc");Q4=makeQuery(id+"F18.imprint","IMPRINT",FACE,{"disambiguationData":[TD([[makeQuery(id+"F18.imprint","IMPRINT",EDGE,{"derivedFrom":subQ0}),1.0]])]});}
            extrude(context, id + "F19", {"entities" : qUnion([Q0, Q1, Q2, Q3, Q4]), "operationType" : NewBodyOperationType.ADD, "depth" : 203.2 * mm});
        }
    });
